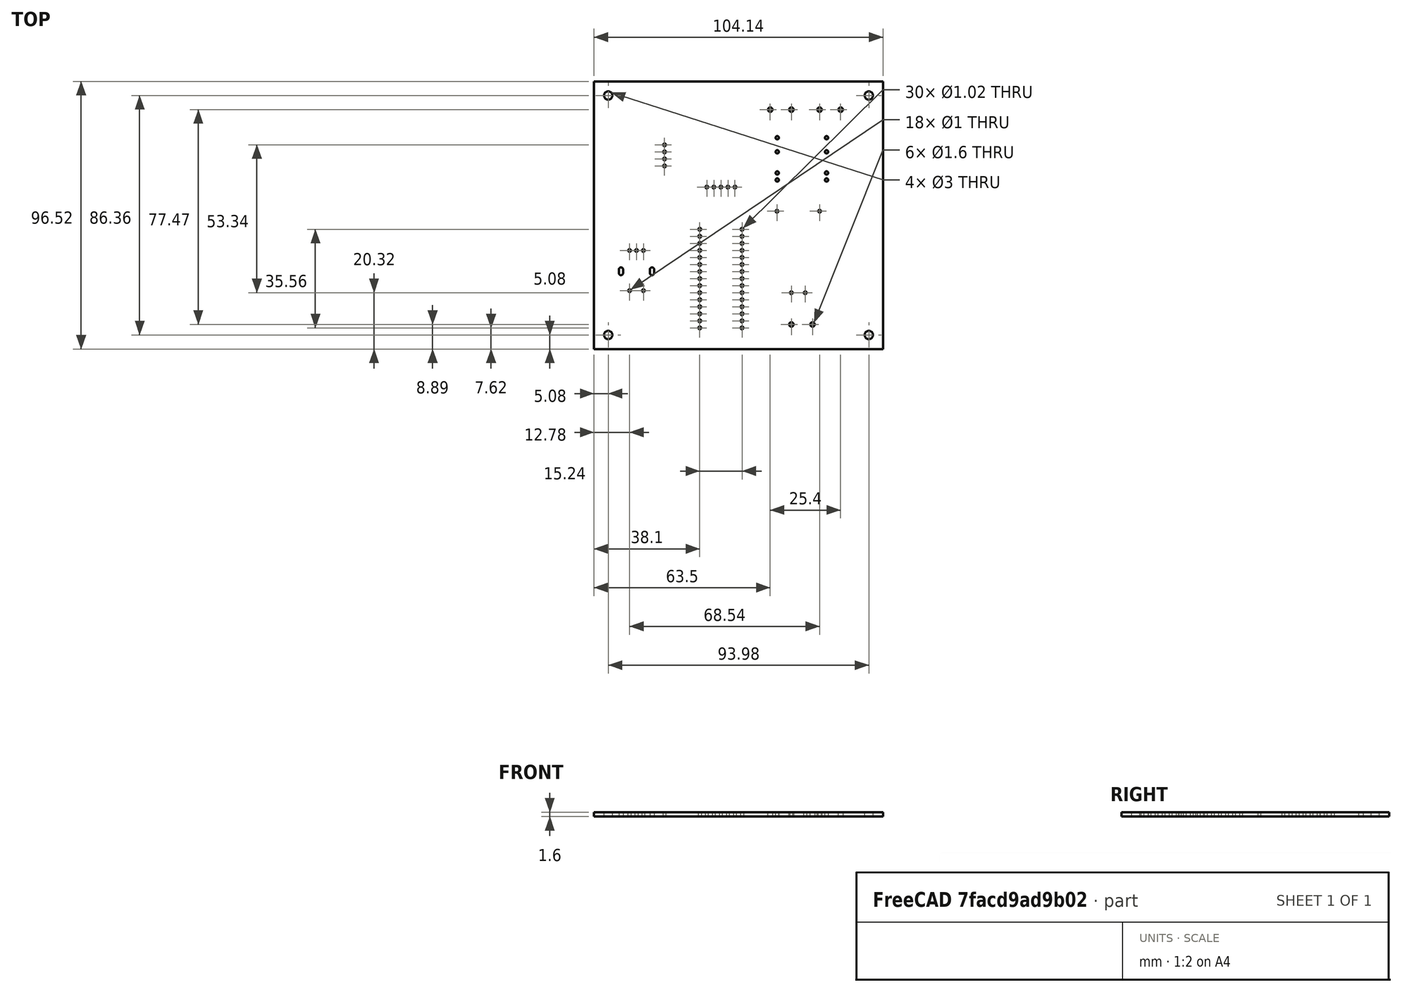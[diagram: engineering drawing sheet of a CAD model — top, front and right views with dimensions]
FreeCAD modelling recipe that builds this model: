
FCSTD DOCUMENT  (FreeCAD 0.18R16110 (Git))
Label: casing_pcb
License: All rights reserved
LicenseURL: http://en.wikipedia.org/wiki/All_rights_reserved
objects: App::Part×4, Part::Feature×1, Sketcher::SketchObject×1
note: 2 computed .brp shape members not serialized (recipe doc carries the construction recipe); baked Part::Feature solids carry a one-line shape summary decoded from their .brp

FEATURE [Part::Feature] Pcb
  Placement = pos=(-139.446,106.807,0) rot=(0,0,1;0rad)
  shape: bbox 104.1 x 96.52 x 1.6 mm, 84 faces (baked)
FEATURE [Sketcher::SketchObject] PCB_Sketch
  sketch-geometry (4):
    g0: LineSegment StartX=66.04 StartY=88.9 StartZ=0 EndX=66.04 EndY=-7.62 EndZ=0
    g1: LineSegment StartX=-38.1 StartY=88.9 StartZ=0 EndX=66.04 EndY=88.9 EndZ=0
    g2: LineSegment StartX=-38.1 StartY=-7.62 StartZ=0 EndX=-38.1 EndY=88.9 EndZ=0
    g3: LineSegment StartX=66.04 StartY=-7.62 StartZ=0 EndX=-38.1 EndY=-7.62 EndZ=0
  constraints (4):
    c: Coincident(g2,g3)
    c: Coincident(g1,g2)
    c: Coincident(g0,g3)
    c: Coincident(g0,g1)
FEATURE [App::Part] Board_Geoms
  Group = -> [Pcb,PCB_Sketch]
  Origin = -> Origin
FEATURE [App::Part] Top
  Origin = -> Origin003
FEATURE [App::Part] Step_Models
  Group = -> [Top]
  Origin = -> Origin002
FEATURE [App::Part] Board  label="SVC_1.0"
  Group = -> [Board_Geoms,Step_Models]
  Origin = -> Origin001
